# Revit family: BRIDA
name_source: partatom
category: Pipe Accessories
units: mm (PartAtom-declared; Revit-internal decimal feet)

## family parameters
Always vertical = Yes
Cut with Voids When Loaded = No
Part Type = Breaks Into
Round Connector Dimension = Use Diameter
Shared = No
Work Plane-Based = No

## types (5) — shared parameters
Description = BRIDAS EN PVC PARA APLICACIONES TIPO LIVIANO Y PESADO
Imagen = https://pcpplasticos.co
Manufacturer = PCP PLASTICOS
URL = https://pcpplasticos.co
zero-valued in all types: Default Elevation

## per-type parameters (varying)
| type | 2" | 3" | 4" | 6" | 8" | D | D1 | D2 | SKU | d1 | d2 |
| 3" | No | Yes | No | No | No | 76 mm | 63 mm | 62 mm | 3087 | 63 mm | 62 mm |
| 4" | No | No | Yes | No | No | 102 mm | 67 mm | 66 mm  [stored 0.216535 ft] | 3089 | 75 mm  [stored 0.246063 ft] | 74 mm |
| 6" | No | No | No | Yes | No | 152 mm | 92 mm  [stored 0.301837 ft] | 91 mm | 3091 | 75 mm  [stored 0.246063 ft] | 74 mm |
| 8" | No | No | No | No | Yes | 203 mm | 118 mm | 117 mm | 3106 | 125 mm  [stored 0.410105 ft] | 124 mm |
| 2" | Yes | No | No | No | No | 51 mm | 41 mm  [stored 0.134514 ft] | 40 mm | 3085 | 41 mm  [stored 0.134514 ft] | 40 mm |

note: [stored X ft] marks values corroborated as IEEE doubles in the binary element streams (Revit-internal decimal feet)

## geometry (parser evidence)
native form markers: Sweep x2
no freeform markers — native parametric forms only
